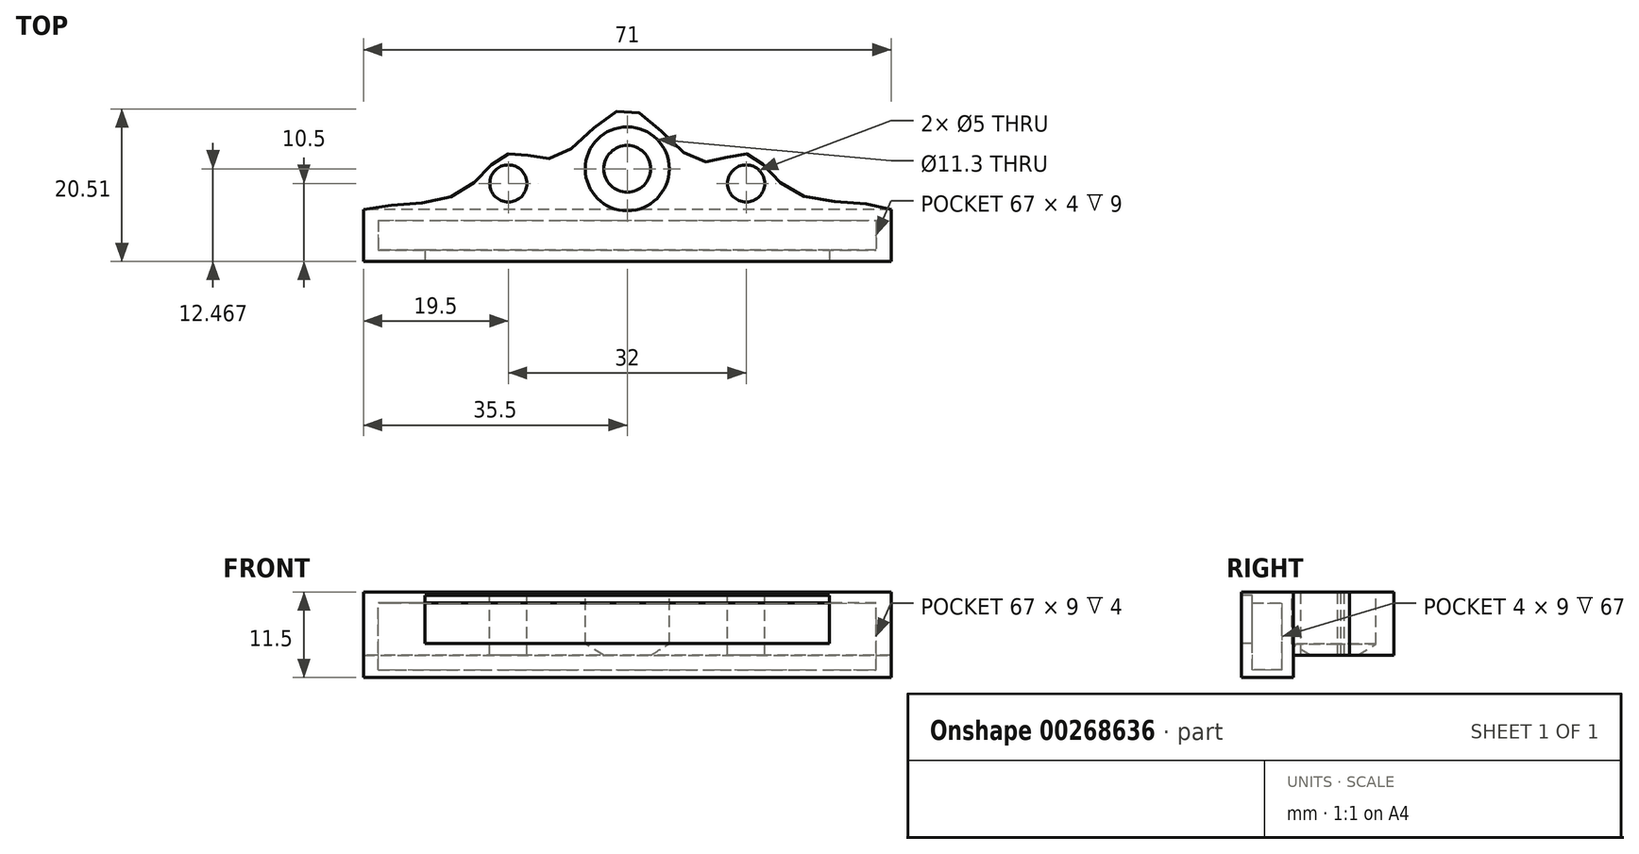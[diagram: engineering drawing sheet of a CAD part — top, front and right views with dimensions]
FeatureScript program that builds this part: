
annotation { "Feature Type Name" : "Feature", "Feature Type Description" : "" }
export const myFeature = defineFeature(function(context is Context, id is Id, definition is map)
    precondition{}
    {
        {
            var Q0;
            Q0=qCreatedBy(makeId("Top.planeOp"),FACE);
            var sketch = newSketch(context, id + "F0", { "sketchPlane" : qUnion([Q0])});
            skLineSegment(sketch, "E0.bottom", {"start": v(35.5, -3.5) * mm, "end": v(-35.5, -3.5) * mm});
            skLineSegment(sketch, "E0.top", {"start": v(35.5, 3.5) * mm, "end": v(-35.5, 3.5) * mm});
            skLineSegment(sketch, "E0.left", {"start": v(35.5, -3.5) * mm, "end": v(35.5, 3.5) * mm});
            skLineSegment(sketch, "E0.right", {"start": v(-35.5, -3.5) * mm, "end": v(-35.5, 3.5) * mm});
            skPoint(sketch, "E0.middle", {"position": v(0, 0) * mm});
            skFitSpline(sketch, "E1", {"points": [v(-35.5, 3.5) * mm, v(-22.6, 5.73) * mm, v(-15.96, 11) * mm, v(-9.44, 10.57) * mm, v(0, 17.01) * mm, v(9.42, 10.08) * mm, v(16.09, 11) * mm, v(22.6, 5.73) * mm, v(35.5, 3.5) * mm], "startDerivative": vector(76.87, 19.5) * mm, "endDerivative": vector(59.53, -29.95) * mm});
            skPoint(sketch, "E2", {"position": v(-16, 7) * mm});
            skPoint(sketch, "E3", {"position": v(0, 8.97) * mm});
            skPoint(sketch, "E4", {"position": v(16, 7) * mm});
            skSolve(sketch);
        }
        {
            var Q0;
            Q0=makeQuery(id+"F0.imprint","IMPRINT",FACE,{"disambiguationData":[TD([[makeQuery(id+"F0.imprint","IMPRINT",EDGE,{"derivedFrom":sQuery(id+"F0.wireOp",EDGE,"E0.bottom")}),-1.0]])]});
            extrude(context, id + "F1", {"entities" : qUnion([Q0]), "oppositeDirection" : true, "depth" : 11.5 * mm});
        }
        {
            var Q0;
            Q0=makeQuery(id+"F0.imprint","IMPRINT",FACE,{"disambiguationData":[TD([[makeQuery(id+"F0.imprint","IMPRINT",EDGE,{"derivedFrom":sQuery(id+"F0.wireOp",EDGE,"E0.top")}),-1.0]])]});
            extrude(context, id + "F2", {"entities" : qUnion([Q0]), "operationType" : NewBodyOperationType.ADD, "oppositeDirection" : true, "depth" : 8.5 * mm, "offsetDistance" : 25 * mm});
        }
        {
            var Q0;
            Q0=sQuery(id+"F0.wireOp",VERTEX,"E3");
            var Q1;
            Q1=makeQuery(id+"F1.opExtrude","SWEPT_BODY",BODY,{"disambiguationData":[OSD([sQuery(id+"F0.wireOp",EDGE,"E0.bottom"),sQuery(id+"F0.wireOp",EDGE,"E0.top"),sQuery(id+"F0.wireOp",EDGE,"E0.left"),sQuery(id+"F0.wireOp",EDGE,"E0.right"),sQuery(id+"F0.wireOp",EDGE,"qSG4pFbB-mWNJ-fMbz-A37t-o3lnEbjPYmPd.bottom"),sQuery(id+"F0.wireOp",EDGE,"qSG4pFbB-mWNJ-fMbz-A37t-o3lnEbjPYmPd.top"),sQuery(id+"F0.wireOp",EDGE,"qSG4pFbB-mWNJ-fMbz-A37t-o3lnEbjPYmPd.left"),sQuery(id+"F0.wireOp",EDGE,"qSG4pFbB-mWNJ-fMbz-A37t-o3lnEbjPYmPd.right")])]});
            hole(context, id + "F3", {"style" : HoleStyle.SIMPLE, "endStyle" : HoleEndStyle.BLIND, "holeDiameter" : 11.3 * mm, "holeDepth" : 7 * mm, "tappedDepth" : 12 * mm, "tapClearance" : 3, "locations" : qUnion([Q0]), "scope" : qUnion([Q1])});
        }
        {
            var Q0;
            Q0=sQuery(id+"F0.wireOp",VERTEX,"E2");
            var Q1;
            Q1=sQuery(id+"F0.wireOp",VERTEX,"E4");
            var Q2;
            Q2=makeQuery(id+"F1.opExtrude","SWEPT_BODY",BODY,{"disambiguationData":[OSD([sQuery(id+"F0.wireOp",EDGE,"E0.bottom"),sQuery(id+"F0.wireOp",EDGE,"E0.top"),sQuery(id+"F0.wireOp",EDGE,"E0.left"),sQuery(id+"F0.wireOp",EDGE,"E0.right"),sQuery(id+"F0.wireOp",EDGE,"qSG4pFbB-mWNJ-fMbz-A37t-o3lnEbjPYmPd.bottom"),sQuery(id+"F0.wireOp",EDGE,"qSG4pFbB-mWNJ-fMbz-A37t-o3lnEbjPYmPd.top"),sQuery(id+"F0.wireOp",EDGE,"qSG4pFbB-mWNJ-fMbz-A37t-o3lnEbjPYmPd.left"),sQuery(id+"F0.wireOp",EDGE,"qSG4pFbB-mWNJ-fMbz-A37t-o3lnEbjPYmPd.right")])]});
            hole(context, id + "F4", {"style" : HoleStyle.SIMPLE, "endStyle" : HoleEndStyle.THROUGH, "holeDiameter" : 5 * mm, "tappedDepth" : 12 * mm, "tapClearance" : 3, "locations" : qUnion([Q0, Q1]), "scope" : qUnion([Q2])});
        }
        {
            var Q0;
            Q0=makeQuery(id+"F1.opExtrude","SWEPT_FACE",FACE,{"disambiguationData":[OSD([sQuery(id+"F0.wireOp",EDGE,"E0.bottom")])]});
            var sketch = newSketch(context, id + "F5", { "sketchPlane" : qUnion([Q0])});
            skLineSegment(sketch, "E5.bottom", {"start": v(27.2, -6.93) * mm, "end": v(-27.2, -6.93) * mm});
            skLineSegment(sketch, "E5.top", {"start": v(27.2, -0.43) * mm, "end": v(-27.2, -0.43) * mm});
            skLineSegment(sketch, "E5.left", {"start": v(27.2, -6.93) * mm, "end": v(27.2, -0.43) * mm});
            skLineSegment(sketch, "E5.right", {"start": v(-27.2, -6.93) * mm, "end": v(-27.2, -0.43) * mm});
            skPoint(sketch, "E5.middle", {"position": v(0, -3.68) * mm});
            skSolve(sketch);
        }
        {
            var Q0;
            Q0=makeQuery(id+"F5.imprint","IMPRINT",FACE,{"disambiguationData":[TD([[makeQuery(id+"F5.imprint","IMPRINT",EDGE,{"derivedFrom":sQuery(id+"F5.wireOp",EDGE,"E5.bottom")}),-1.0]])]});
            extrude(context, id + "F6", {"entities" : qUnion([Q0]), "operationType" : NewBodyOperationType.REMOVE, "oppositeDirection" : true, "depth" : 2 * mm});
        }
        {
            var Q0;
            Q0=makeQuery(id+"F0.imprint","IMPRINT",FACE,{"disambiguationData":[TD([[makeQuery(id+"F0.imprint","IMPRINT",EDGE,{"derivedFrom":sQuery(id+"F0.wireOp",EDGE,"E0.bottom")}),-1.0]])]});
            var sketch = newSketch(context, id + "F7", { "sketchPlane" : qUnion([Q0])});
            skLineSegment(sketch, "E6.bottom", {"start": v(33.5, -2) * mm, "end": v(-33.5, -2) * mm});
            skLineSegment(sketch, "E6.top", {"start": v(33.5, 2) * mm, "end": v(-33.5, 2) * mm});
            skLineSegment(sketch, "E6.left", {"start": v(33.5, -2) * mm, "end": v(33.5, 2) * mm});
            skLineSegment(sketch, "E6.right", {"start": v(-33.5, -2) * mm, "end": v(-33.5, 2) * mm});
            skPoint(sketch, "E6.middle", {"position": v(0, 0) * mm});
            skSolve(sketch);
        }
        {
            var Q0;
            Q0=makeQuery(id+"F7.imprint","IMPRINT",FACE,{"disambiguationData":[TD([[makeQuery(id+"F7.imprint","IMPRINT",EDGE,{"derivedFrom":sQuery(id+"F7.wireOp",EDGE,"E6.bottom")}),-1.0]])]});
            extrude(context, id + "F8", {"entities" : qUnion([Q0]), "operationType" : NewBodyOperationType.REMOVE, "oppositeDirection" : true, "depth" : 11 * mm});
        }
        {
            var Q0;
            Q0=makeQuery(id+"F7.imprint","IMPRINT",FACE,{"disambiguationData":[TD([[makeQuery(id+"F7.imprint","IMPRINT",EDGE,{"derivedFrom":sQuery(id+"F7.wireOp",EDGE,"E6.bottom")}),-1.0]])]});
            extrude(context, id + "F9", {"entities" : qUnion([Q0]), "operationType" : NewBodyOperationType.ADD, "oppositeDirection" : true, "depth" : 1.5 * mm});
        }
        {
            var Q0;
            Q0=makeQuery(id+"F8.boolean.opBoolean","COPY",FACE,{"derivedFrom":makeQuery(id+"F8.opExtrude","SWEPT_FACE",FACE,{"disambiguationData":[OSD([sQuery(id+"F7.wireOp",EDGE,"E6.top")])]})});
            var sketch = newSketch(context, id + "F10", { "sketchPlane" : qUnion([Q0])});
            skLineSegment(sketch, "E7.bottom", {"start": v(37.5, -4.1) * mm, "end": v(-37.5, -4.1) * mm});
            skLineSegment(sketch, "E7.top", {"start": v(37.5, -4) * mm, "end": v(-37.5, -4) * mm});
            skLineSegment(sketch, "E7.left", {"start": v(37.5, -4.1) * mm, "end": v(37.5, -4) * mm});
            skLineSegment(sketch, "E7.right", {"start": v(-37.5, -4.1) * mm, "end": v(-37.5, -4) * mm});
            skPoint(sketch, "E7.middle", {"position": v(0, -4.05) * mm});
            skSolve(sketch);
        }
        {
            var Q0;
            Q0=makeQuery(id+"F1.opExtrude","CAP_FACE",FACE,{"disambiguationData":[OSD([sQuery(id+"F0.wireOp",EDGE,"E0.bottom"),sQuery(id+"F0.wireOp",EDGE,"E0.top"),sQuery(id+"F0.wireOp",EDGE,"E0.left"),sQuery(id+"F0.wireOp",EDGE,"E0.right")])],"isStart":false});
            extrude(context, id + "F11", {"entities" : qUnion([Q0]), "operationType" : NewBodyOperationType.ADD, "oppositeDirection" : true, "depth" : 1 * mm});
        }
    });
